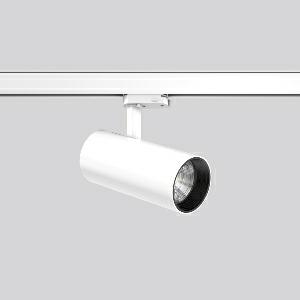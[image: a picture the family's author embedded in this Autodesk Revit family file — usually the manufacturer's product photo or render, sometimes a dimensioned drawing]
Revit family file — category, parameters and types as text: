
# Revit family: deecos_s_mini_742200_002_3_76_2090
name_source: partatom
category: Lighting Fixtures
units: mm (PartAtom-declared; Revit-internal decimal feet)

## family parameters
Cut with Voids When Loaded = No
Host = Face
Light Source = No
Part Type = Normal
Room Calculation Point = No
Round Connector Dimension = Use Diameter
Shared = No

## types (1)
- DEECOS S mini (1 x LED Modul 935, 2000 lm, 3500)
    Apparent Load = 20 VA
    Approval mark = CE
    CIE Flux Codes = 98 100 100 100 100
    Color Rendering = 92
    Color Temperature = 3500
    Default Elevation = 1800 mm
    Description = Series: DEECOS S mini
LED surface-mounted projector in modern design with no visible cooling ribs. Housing: die-cast aluminium, powder-coated. Rotation range: 356°. Swivel range: 90°. Black plastic ring and recessed LED to prevent glare from the side. Optical assembly with lens made of plastic (polycarbonate) for the best homogeneous light distribution - can be changed without tools. Best colour rendering index Ra>90. With adapter for RZB 3-circuit DALI tracks. Suitable for Track on ceiling, Wall track. High quality converter without flickering and stroboscopic effect. The following accessories can be mounted without use of tools: interchangeable lenses, decorative glasses, honeycomb louvre, clear and frosted diffusers, white interchangeable plastic ring. 
Colour: traffic white, matt (RAL 9016)
Diameter: 87 mm
Height: 214 mm
Lamp: LED
Socket: without socket
Colour temperature: 3500K
Colour rendering index (CRI): 92
System power: 20 W
Rated luminous flux: 2000 lm
Luminous efficiency: 100 lm/W
Control gear: Converter, dimmable, DALI
Protection class: I
Type of protection: IP 20
    Height = 214 mm
    Lamp = 1 x LED Modul 935
    Lamp Light Flux = 2000 lm
    Lamp count = 1
    Length = 87 mm
    Lifetime = 50000 h
    Luminous efficacy = 100 lm/W
    Manufacturer = RZB
    ModVariant = No
    Model = 742200.002.3.76
    Mounting Place = Ceiling
    Mounting Type = Rail mounted
    Number of Poles = 1
    OnlyDefault = Yes
    Power Factor = 1
    Product Name = DEECOS S mini
    Product group = Track mounted projectors
    ProductGroupID = 301
    Protection Class = Protection class I
    Protection Degree = IP 20
    RLX_Detail_Level = 1
    RLX_Emergency_Light_Flux = 0 lm
    RLX_Emergency_Type = 0
    RLX_Emergency_Type_DB = No
    RlxData = <blob elided: 35189 chars, md5=2a678e97>
    Socket = socket
    Standby Power = 0 W
    System Light Flux = 2000 lm
    System Power = 20 W
    Type Comments = Product without accessories
    Type Image = 741930.002.jpg
    URL = http://relux.com
    VarID = ---
    Voltage = 230 V
    Voltage Range = 220-240 V
    Weight = 0.00 kg
    Width = 0 mm  [stored 0 ft]

note: [stored X ft] marks values corroborated as IEEE doubles in the binary element streams (Revit-internal decimal feet)

## geometry (parser evidence)
native form markers: Blend x4, Sweep x12
no freeform markers — native parametric forms only
